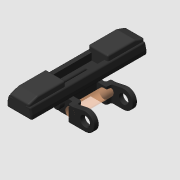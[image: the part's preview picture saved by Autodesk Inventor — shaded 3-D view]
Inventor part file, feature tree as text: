
AUTODESK INVENTOR PART (.ipt)
format: ipt  version: 2021 (Build 250183000, 183)  size: 668,160 bytes
history: native  units: in
note: dims shown in document units (in); Inventor stores cm internally (conversion verified against a paired STEP export)
features: other x4, sketch x3, extrude x3, imported_body x1
ambient origin geometry x8: Origin, YZ Plane, XZ Plane, XY Plane, X Axis, Y Axis, Z Axis, Center Point
bodies: Body1 (feature_tree), Body2 (feature_tree), Body3 (feature_tree), Body4 (feature_tree)
feature tree (11):
  parser-record x1  (decoder bookkeeping rows leaked as tree rows — omitted from the tree; the rows remain in map.json)
  imported_body  "Base1"
  sketch  "Sketch1"  dims[d0=0.118in d1=0.063in d2=0.0in]
  other  "Srf1"
  sketch  "Sketch2"  dims[d3=0.0in d4=0.118in]
  other  "Srf2"
  sketch  "Sketch3"  dims[d5=0.063in d6=0.0in d7=0.0in d8=0.0in d9=0.0in d10=0.125in d11=1.0in d12=0.0in]
  other  "Srf3"
  extrude  "ExtrusionSrf1"  Depth=0.063in TaperAngle=0.0deg
  extrude  "ExtrusionSrf2"  Depth=0.118in
  extrude  "ExtrusionSrf3"  TaperAngle=0.0deg  [1 undecoded]
note: 1 required parameter value undecoded (feature->parameter linkage not recoverable at this tier; creation-order binding heuristic only, values carry confidence <= 0.55)
